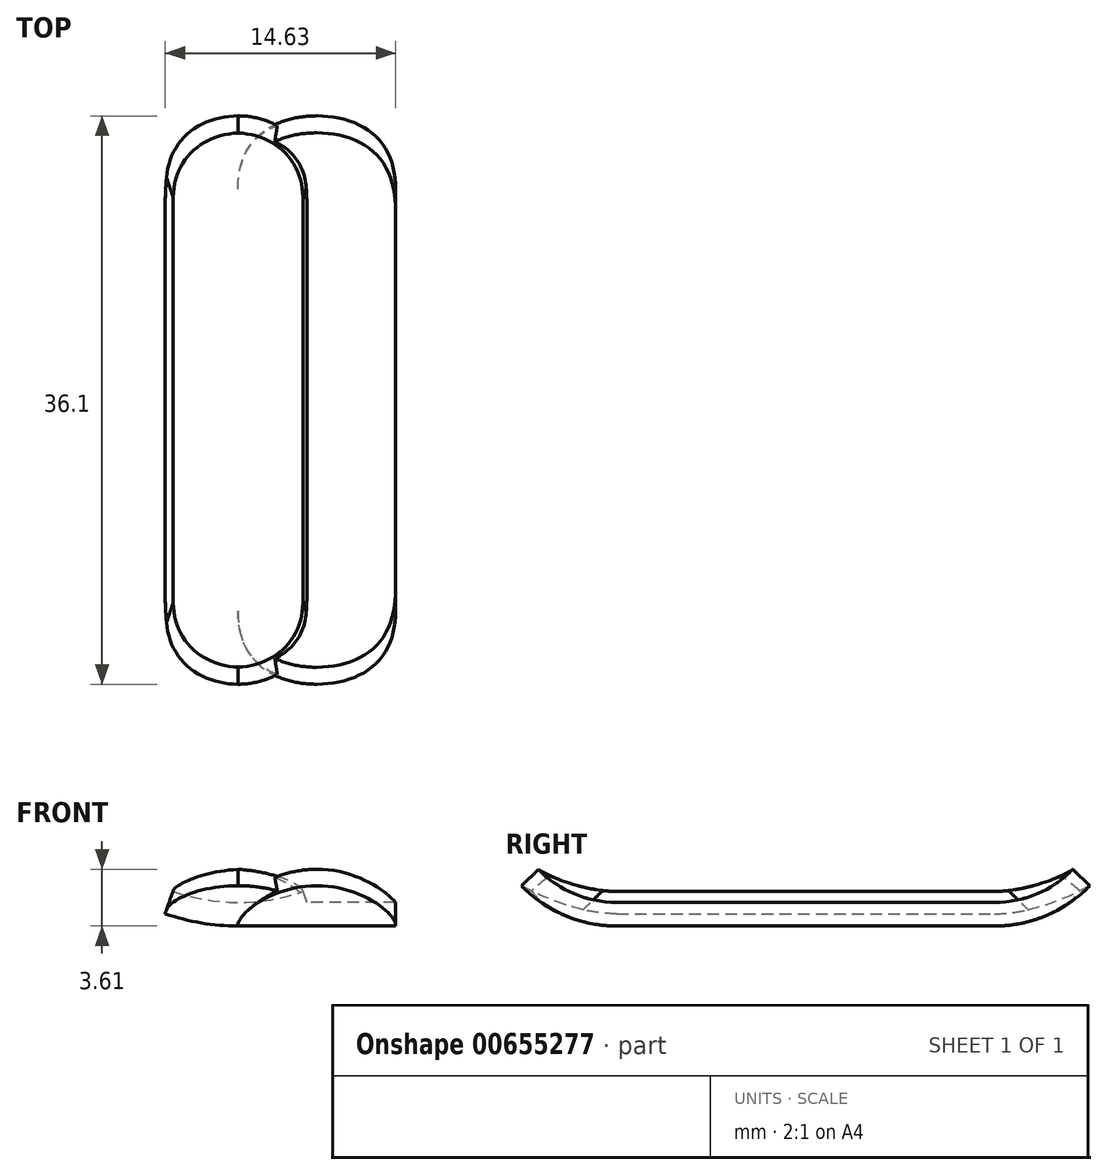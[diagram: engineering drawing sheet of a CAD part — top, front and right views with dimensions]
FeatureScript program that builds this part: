
annotation { "Feature Type Name" : "Feature", "Feature Type Description" : "" }
export const myFeature = defineFeature(function(context is Context, id is Id, definition is map)
    precondition{}
    {
        {
            var Q0;
            Q0=qCreatedBy(makeId("Right.planeOp"),FACE);
            var sketch = newSketch(context, id + "F0", { "sketchPlane" : qUnion([Q0])});
            skLineSegment(sketch, "E0.bottom", {"start": v(0, 0) * mm, "end": v(12, 0) * mm});
            skLineSegment(sketch, "E0.top", {"start": v(0, 1.5) * mm, "end": v(12, 1.5) * mm});
            skLineSegment(sketch, "E0.left", {"start": v(0, 0) * mm, "end": v(0, 1.5) * mm});
            skLineSegment(sketch, "E0.right", {"start": v(12, 0) * mm, "end": v(12, 1.5) * mm, "construction": true});
            skArc(sketch, "E1", {"start": v(12, 1.5) * mm, "mid": v(14.7, 2.05) * mm, "end": v(16.97, 3.6) * mm});
            skArc(sketch, "E2", {"start": v(12, 0) * mm, "mid": v(15.29, 0.67) * mm, "end": v(18.05, 2.56) * mm});
            skLineSegment(sketch, "E3", {"start": v(16.97, 3.6) * mm, "end": v(18.05, 2.56) * mm});
            skSolve(sketch);
        }
        {
            var Q0;
            Q0=qCreatedBy(makeId("Front.planeOp"),FACE);
            var sketch = newSketch(context, id + "F1", { "sketchPlane" : qUnion([Q0])});
            skArc(sketch, "E4", {"start": v(0, 0) * mm, "mid": v(2.35, 0.2) * mm, "end": v(4.63, 0.78) * mm});
            skLineSegment(sketch, "E5", {"start": v(0, 0) * mm, "end": v(-3.93, 0) * mm, "construction": true});
            skSolve(sketch);
        }
        {
            var Q0;
            Q0=makeQuery(id+"F0.imprint","IMPRINT",FACE,{"disambiguationData":[TD([[makeQuery(id+"F0.imprint","IMPRINT",EDGE,{"derivedFrom":sQuery(id+"F0.wireOp",EDGE,"E0.bottom")}),1.0]])]});
            var Q1;
            Q1=sQuery(id+"F1.wireOp",EDGE,"E4");
            sweep(context, id + "F2", {"profiles" : qUnion([Q0]), "path" : qUnion([Q1])});
        }
        {
            var Q0;
            Q0=makeQuery(id+"F2.opSweep","SWEPT_BODY",BODY,{"disambiguationData":[OSD([sQuery(id+"F0.wireOp",EDGE,"E0.bottom"),sQuery(id+"F0.wireOp",EDGE,"E0.top"),sQuery(id+"F0.wireOp",EDGE,"E0.left"),sQuery(id+"F0.wireOp",EDGE,"E1"),sQuery(id+"F0.wireOp",EDGE,"E2"),sQuery(id+"F0.wireOp",EDGE,"E3"),sQuery(id+"F1.wireOp",EDGE,"E4")])]});
            var Q1;
            Q1=makeQuery(id+"F2.opSweep","CAP_FACE",FACE,{"disambiguationData":[OSD([sQuery(id+"F0.wireOp",EDGE,"E0.bottom"),sQuery(id+"F0.wireOp",EDGE,"E0.top"),sQuery(id+"F0.wireOp",EDGE,"E0.left"),sQuery(id+"F0.wireOp",EDGE,"E1"),sQuery(id+"F0.wireOp",EDGE,"E2"),sQuery(id+"F0.wireOp",EDGE,"E3"),sQuery(id+"F1.wireOp",VERTEX,"E4.start")])],"isStart":true});
            mirror(context, id + "F3", {"operationType" : NewBodyOperationType.ADD, "entities" : qUnion([Q0]), "mirrorPlane" : qUnion([Q1])});
        }
        {
            var Q0;
            Q0=makeQuery(id+"F2.opSweep","CAP_EDGE",EDGE,{"disambiguationData":[OSD([sQuery(id+"F0.wireOp",EDGE,"E3"),sQuery(id+"F1.wireOp",VERTEX,"E4.end")])],"isStart":false});
            var Q1;
            Q1=makeQuery(id+"F3.opPattern","COPY",EDGE,{"derivedFrom":makeQuery(id+"F2.opSweep","CAP_EDGE",EDGE,{"disambiguationData":[OSD([sQuery(id+"F0.wireOp",EDGE,"E3"),sQuery(id+"F1.wireOp",VERTEX,"E4.end")])],"isStart":false}),"instanceName":"1"});
            fillet(context, id + "F4", {"entities" : qUnion([Q0, Q1]), "radius" : 5 * mm, "tangentPropagation" : true, "allowEdgeOverflow" : false});
        }
        {
            var Q0;
            Q0=makeQuery(id+"F2.opSweep","SWEPT_BODY",BODY,{"disambiguationData":[OSD([sQuery(id+"F0.wireOp",EDGE,"E0.bottom"),sQuery(id+"F0.wireOp",EDGE,"E0.top"),sQuery(id+"F0.wireOp",EDGE,"E0.left"),sQuery(id+"F0.wireOp",EDGE,"E1"),sQuery(id+"F0.wireOp",EDGE,"E2"),sQuery(id+"F0.wireOp",EDGE,"E3"),sQuery(id+"F1.wireOp",EDGE,"E4")])]});
            var Q1;
            {var subQ0=makeQuery(id+"F2.opSweep","SWEPT_FACE",FACE,{"disambiguationData":[OSD([sQuery(id+"F0.wireOp",EDGE,"E0.left"),sQuery(id+"F1.wireOp",EDGE,"E4")])]});Q1=makeQuery(id+"F3.boolean.opBoolean","MERGE",FACE,{"derivedFrom":[subQ0,makeQuery(id+"F3.opPattern","COPY",FACE,{"derivedFrom":subQ0,"instanceName":"1"})]});}
            mirror(context, id + "F5", {"operationType" : NewBodyOperationType.ADD, "entities" : qUnion([Q0]), "mirrorPlane" : qUnion([Q1])});
        }
        {
            var Q0;
            Q0=makeQuery(id+"F0.imprint","IMPRINT",FACE,{"disambiguationData":[TD([[makeQuery(id+"F0.imprint","IMPRINT",EDGE,{"derivedFrom":sQuery(id+"F0.wireOp",EDGE,"E0.bottom")}),1.0]])]});
            extrude(context, id + "F6", {"entities" : qUnion([Q0]), "depth" : 10 * mm, "offsetDistance" : 25 * mm});
        }
        {
            var Q0;
            Q0=makeQuery(id+"F6.opExtrude","CAP_EDGE",EDGE,{"disambiguationData":[OSD([sQuery(id+"F0.wireOp",EDGE,"E3")])],"isStart":true});
            var Q1;
            Q1=makeQuery(id+"F6.opExtrude","CAP_EDGE",EDGE,{"disambiguationData":[OSD([sQuery(id+"F0.wireOp",EDGE,"E3")])],"isStart":false});
            fillet(context, id + "F7", {"entities" : qUnion([Q0, Q1]), "radius" : 5 * mm, "tangentPropagation" : true, "allowEdgeOverflow" : false});
        }
        {
            var Q0;
            Q0=makeQuery(id+"F6.opExtrude","SWEPT_BODY",BODY,{"disambiguationData":[OSD([sQuery(id+"F0.wireOp",EDGE,"E0.bottom"),sQuery(id+"F0.wireOp",EDGE,"E0.top"),sQuery(id+"F0.wireOp",EDGE,"E0.left"),sQuery(id+"F0.wireOp",EDGE,"E1"),sQuery(id+"F0.wireOp",EDGE,"E2"),sQuery(id+"F0.wireOp",EDGE,"E3")])]});
            var Q1;
            Q1=makeQuery(id+"F6.opExtrude","SWEPT_FACE",FACE,{"disambiguationData":[OSD([sQuery(id+"F0.wireOp",EDGE,"E0.left")])]});
            mirror(context, id + "F8", {"operationType" : NewBodyOperationType.ADD, "entities" : qUnion([Q0]), "mirrorPlane" : qUnion([Q1])});
        }
    });
